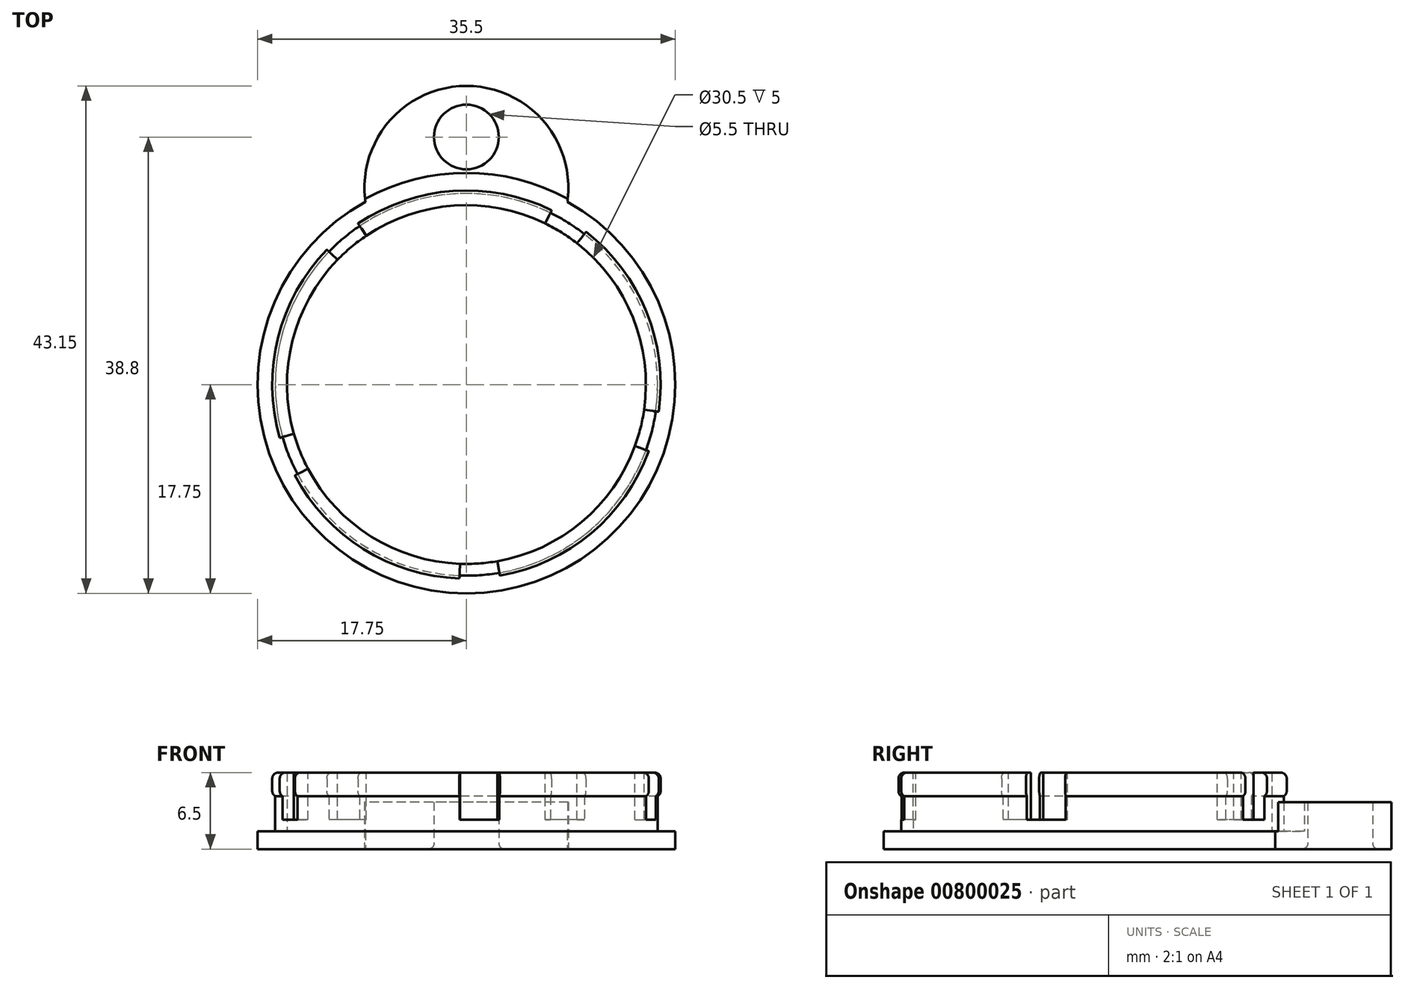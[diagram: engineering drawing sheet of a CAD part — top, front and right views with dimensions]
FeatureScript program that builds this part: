
annotation { "Feature Type Name" : "Feature", "Feature Type Description" : "" }
export const myFeature = defineFeature(function(context is Context, id is Id, definition is map)
    precondition{}
    {
        {
            var Q0;
            Q0=qCreatedBy(makeId("Top.planeOp"),FACE);
            var sketch = newSketch(context, id + "F0", { "sketchPlane" : qUnion([Q0])});
            skCircle(sketch, "E0", {"center": v(0, 0) * mm, "radius": 17.75 * mm});
            skLineSegment(sketch, "E1", {"start": v(-30.05, 0) * mm, "end": v(29.32, 0) * mm, "construction": true});
            skLineSegment(sketch, "E2", {"start": v(0, 26.58) * mm, "end": v(0, -26.58) * mm, "construction": true});
            skArc(sketch, "E3", {"start": v(0, 25.4) * mm, "mid": v(-6.53, 22.42) * mm, "end": v(-8.58, 15.54) * mm});
            skArc(sketch, "E4.MirrorCS", {"start": v(0, 25.4) * mm, "mid": v(6.53, 22.42) * mm, "end": v(8.58, 15.54) * mm});
            skCircle(sketch, "E5", {"center": v(0, 21.05) * mm, "radius": 2.75 * mm});
            skSolve(sketch);
        }
        {
            var Q0;
            {var subQ0=sQuery(id+"F0.wireOp",EDGE,"E0");var subQ1=makeQuery(id+"F0.imprint","INTERSECT",VERTEX,{"derivedFrom":[subQ0,sQuery(id+"F0.wireOp",EDGE,"E3")]});Q0=makeQuery(id+"F0.imprint","IMPRINT",FACE,{"disambiguationData":[TD([[makeQuery(id+"F0.imprint","IMPRINT",EDGE,{"disambiguationData":[TD([[subQ1,1.0]])],"derivedFrom":subQ0}),1.0]])]});}
            var Q1;
            {var subQ0=sQuery(id+"F0.wireOp",EDGE,"E3");Q1=makeQuery(id+"F0.imprint","IMPRINT",FACE,{"disambiguationData":[TD([[makeQuery(id+"F0.imprint","IMPRINT",EDGE,{"derivedFrom":subQ0}),1.0]])]});}
            extrude(context, id + "F1", {"entities" : qUnion([Q0, Q1]), "depth" : 1.5 * mm, "offsetDistance" : 25 * mm});
        }
        {
            var Q0;
            Q0=makeQuery(id+"F1.opExtrude","CAP_FACE",FACE,{"disambiguationData":[OSD([sQuery(id+"F0.wireOp",EDGE,"E0"),sQuery(id+"F0.wireOp",EDGE,"E3"),sQuery(id+"F0.wireOp",EDGE,"E4.MirrorCS"),sQuery(id+"F0.wireOp",EDGE,"E5")])],"isStart":false});
            var sketch = newSketch(context, id + "F2", { "sketchPlane" : qUnion([Q0])});
            skCircle(sketch, "E6", {"center": v(0, 0) * mm, "radius": 15.25 * mm});
            skCircle(sketch, "E7", {"center": v(0, 0) * mm, "radius": 16.25 * mm});
            skSolve(sketch);
        }
        {
            var Q0;
            Q0=makeQuery(id+"F2.imprint","IMPRINT",FACE,{"disambiguationData":[TD([[makeQuery(id+"F2.imprint","IMPRINT",EDGE,{"derivedFrom":sQuery(id+"F2.wireOp",EDGE,"E6")}),-1.0]])]});
            extrude(context, id + "F3", {"entities" : qUnion([Q0]), "operationType" : NewBodyOperationType.ADD, "depth" : 3 * mm, "offsetDistance" : 25 * mm});
        }
        {
            var Q0;
            {var subQ0=sQuery(id+"F0.wireOp",EDGE,"E0");var subQ1=sQuery(id+"F0.wireOp",EDGE,"E4.MirrorCS");var subQ2=sQuery(id+"F0.wireOp",EDGE,"E3");var subQ3=sQuery(id+"F0.wireOp",EDGE,"E5");Q0=makeQuery(id+"F3.boolean.opBoolean","SPLIT",FACE,{"disambiguationData":[TD([makeQuery(id+"F1.opExtrude","SWEPT_FACE",FACE,{"disambiguationData":[OSD([subQ0])]})])],"derivedFrom":makeQuery(id+"F1.opExtrude","CAP_FACE",FACE,{"disambiguationData":[OSD([subQ0,subQ2,subQ1,subQ3])],"isStart":false})});}
            var sketch = newSketch(context, id + "F4", { "sketchPlane" : qUnion([Q0])});
            skArc(sketch, "E8", {"start": v(8.58, 15.54) * mm, "mid": v(0, 25.4) * mm, "end": v(-8.58, 15.54) * mm});
            skArc(sketch, "E9", {"start": v(8.61, 15.8) * mm, "mid": v(0, 18) * mm, "end": v(-8.61, 15.8) * mm});
            skSolve(sketch);
        }
        {
            var Q0;
            {var subQ0=sQuery(id+"F4.wireOp",EDGE,"E9");Q0=makeQuery(id+"F4.imprint","IMPRINT",FACE,{"disambiguationData":[TD([[makeQuery(id+"F4.imprint","IMPRINT",EDGE,{"derivedFrom":subQ0}),-1.0]])]});}
            extrude(context, id + "F5", {"entities" : qUnion([Q0]), "operationType" : NewBodyOperationType.ADD, "depth" : 2.5 * mm, "offsetDistance" : 25 * mm});
        }
        {
            var Q0;
            Q0=makeQuery(id+"F3.opExtrude","CAP_FACE",FACE,{"disambiguationData":[OSD([sQuery(id+"F2.wireOp",EDGE,"E6"),sQuery(id+"F2.wireOp",EDGE,"E7")])],"isStart":false});
            var sketch = newSketch(context, id + "F6", { "sketchPlane" : qUnion([Q0])});
            skCircle(sketch, "E10", {"center": v(0, 0) * mm, "radius": 15.25 * mm});
            skCircle(sketch, "E11", {"center": v(0, 0) * mm, "radius": 16.5 * mm});
            skSolve(sketch);
        }
        {
            var Q0;
            Q0=makeQuery(id+"F6.imprint","IMPRINT",FACE,{"disambiguationData":[TD([[makeQuery(id+"F6.imprint","IMPRINT",EDGE,{"derivedFrom":sQuery(id+"F6.wireOp",EDGE,"E10")}),-1.0]])]});
            var Q1;
            Q1=makeQuery(id+"F6.imprint","IMPRINT",FACE,{"disambiguationData":[TD([[makeQuery(id+"F6.imprint","IMPRINT",EDGE,{"derivedFrom":sQuery(id+"F6.wireOp",EDGE,"E11")}),1.0]])]});
            extrude(context, id + "F7", {"entities" : qUnion([Q0, Q1]), "operationType" : NewBodyOperationType.ADD, "depth" : 2 * mm, "offsetDistance" : 25 * mm});
        }
        {
            var Q0;
            Q0=makeQuery(id+"F7.opExtrude","CAP_EDGE",EDGE,{"disambiguationData":[OSD([sQuery(id+"F6.wireOp",EDGE,"E11")])],"isStart":false});
            var Q1;
            Q1=makeQuery(id+"F7.opExtrude","CAP_EDGE",EDGE,{"disambiguationData":[OSD([sQuery(id+"F6.wireOp",EDGE,"E11")])],"isStart":true});
            fillet(context, id + "F8", {"entities" : qUnion([Q0, Q1]), "radius" : 0.5 * mm, "tangentPropagation" : true, "allowEdgeOverflow" : false});
        }
        {
            var Q0;
            Q0=makeQuery(id+"F7.opExtrude","CAP_FACE",FACE,{"disambiguationData":[OSD([sQuery(id+"F6.wireOp",EDGE,"E10"),sQuery(id+"F6.wireOp",EDGE,"E11")])],"isStart":false});
            var sketch = newSketch(context, id + "F9", { "sketchPlane" : qUnion([Q0])});
            skCircle(sketch, "E12.cCircle", {"center": v(0, 0) * mm, "radius": 17.3 * mm, "construction": true});
            skLineSegment(sketch, "E12.0", {"start": v(-14.74, 9.23) * mm, "end": v(-12.5, 12.1) * mm});
            skLineSegment(sketch, "E12.1", {"start": v(-12.5, 12.1) * mm, "end": v(-9.71, 14.43) * mm});
            skLineSegment(sketch, "E12.2", {"start": v(-9.71, 14.43) * mm, "end": v(-6.5, 16.13) * mm});
            skLineSegment(sketch, "E12.3", {"start": v(-6.5, 16.13) * mm, "end": v(-3, 17.13) * mm});
            skLineSegment(sketch, "E12.4", {"start": v(-3, 17.13) * mm, "end": v(0.63, 17.38) * mm});
            skLineSegment(sketch, "E12.5", {"start": v(0.63, 17.38) * mm, "end": v(4.23, 16.87) * mm});
            skLineSegment(sketch, "E12.6", {"start": v(4.23, 16.87) * mm, "end": v(7.64, 15.62) * mm});
            skLineSegment(sketch, "E12.7", {"start": v(7.64, 15.62) * mm, "end": v(10.72, 13.7) * mm});
            skLineSegment(sketch, "E12.8", {"start": v(10.72, 13.7) * mm, "end": v(13.34, 11.17) * mm});
            skLineSegment(sketch, "E12.9", {"start": v(13.34, 11.17) * mm, "end": v(15.37, 8.15) * mm});
            skLineSegment(sketch, "E12.10", {"start": v(15.37, 8.15) * mm, "end": v(16.73, 4.78) * mm});
            skLineSegment(sketch, "E12.11", {"start": v(16.73, 4.78) * mm, "end": v(17.35, 1.2) * mm});
            skLineSegment(sketch, "E12.12", {"start": v(17.35, 1.2) * mm, "end": v(17.22, -2.44) * mm});
            skLineSegment(sketch, "E12.13", {"start": v(17.22, -2.44) * mm, "end": v(16.34, -5.97) * mm});
            skLineSegment(sketch, "E12.14", {"start": v(16.34, -5.97) * mm, "end": v(14.74, -9.23) * mm});
            skLineSegment(sketch, "E12.15", {"start": v(14.74, -9.23) * mm, "end": v(12.5, -12.1) * mm});
            skLineSegment(sketch, "E12.16", {"start": v(12.5, -12.1) * mm, "end": v(9.71, -14.43) * mm});
            skLineSegment(sketch, "E12.17", {"start": v(9.71, -14.43) * mm, "end": v(6.5, -16.13) * mm});
            skLineSegment(sketch, "E12.18", {"start": v(6.5, -16.13) * mm, "end": v(3, -17.13) * mm});
            skLineSegment(sketch, "E12.19", {"start": v(3, -17.13) * mm, "end": v(-0.63, -17.38) * mm});
            skLineSegment(sketch, "E12.20", {"start": v(-0.63, -17.38) * mm, "end": v(-4.23, -16.87) * mm});
            skLineSegment(sketch, "E12.21", {"start": v(-4.23, -16.87) * mm, "end": v(-7.64, -15.62) * mm});
            skLineSegment(sketch, "E12.22", {"start": v(-7.64, -15.62) * mm, "end": v(-10.72, -13.7) * mm});
            skLineSegment(sketch, "E12.23", {"start": v(-10.72, -13.7) * mm, "end": v(-13.34, -11.17) * mm});
            skLineSegment(sketch, "E12.24", {"start": v(-13.34, -11.17) * mm, "end": v(-15.37, -8.15) * mm});
            skLineSegment(sketch, "E12.25", {"start": v(-15.37, -8.15) * mm, "end": v(-16.73, -4.78) * mm});
            skLineSegment(sketch, "E12.26", {"start": v(-16.73, -4.78) * mm, "end": v(-17.35, -1.2) * mm});
            skLineSegment(sketch, "E12.27", {"start": v(-17.35, -1.2) * mm, "end": v(-17.22, 2.44) * mm});
            skLineSegment(sketch, "E12.28", {"start": v(-17.22, 2.44) * mm, "end": v(-16.34, 5.97) * mm});
            skLineSegment(sketch, "E12.29", {"start": v(-16.34, 5.97) * mm, "end": v(-14.74, 9.23) * mm});
            skPoint(sketch, "E12.0.midPoint", {"position": v(-13.62, 10.67) * mm});
            skLineSegment(sketch, "E13", {"start": v(0, 0) * mm, "end": v(0.63, 21) * mm});
            skLineSegment(sketch, "E14", {"start": v(0, 0) * mm, "end": v(4.23, 16.87) * mm});
            skLineSegment(sketch, "E15", {"start": v(0, 0) * mm, "end": v(7.64, 15.62) * mm});
            skLineSegment(sketch, "E16", {"start": v(0, 0) * mm, "end": v(10.72, 13.7) * mm});
            skLineSegment(sketch, "E17", {"start": v(0, 0) * mm, "end": v(13.34, 11.17) * mm});
            skLineSegment(sketch, "E18", {"start": v(0, 0) * mm, "end": v(15.37, 8.15) * mm});
            skLineSegment(sketch, "E19", {"start": v(0, 0) * mm, "end": v(16.73, 4.78) * mm});
            skLineSegment(sketch, "E20", {"start": v(0, 0) * mm, "end": v(17.35, 1.2) * mm});
            skLineSegment(sketch, "E21", {"start": v(0, 0) * mm, "end": v(17.22, -2.44) * mm});
            skLineSegment(sketch, "E22", {"start": v(0, 0) * mm, "end": v(16.34, -5.97) * mm});
            skLineSegment(sketch, "E23", {"start": v(0, 0) * mm, "end": v(14.74, -9.23) * mm});
            skLineSegment(sketch, "E24", {"start": v(0, 0) * mm, "end": v(12.5, -12.1) * mm});
            skLineSegment(sketch, "E25", {"start": v(0, 0) * mm, "end": v(9.71, -14.43) * mm});
            skLineSegment(sketch, "E26", {"start": v(0, 0) * mm, "end": v(6.5, -16.13) * mm});
            skLineSegment(sketch, "E27", {"start": v(0, 0) * mm, "end": v(3, -17.13) * mm});
            skLineSegment(sketch, "E28", {"start": v(0, 0) * mm, "end": v(-0.63, -17.38) * mm});
            skLineSegment(sketch, "E29", {"start": v(0, 0) * mm, "end": v(-4.23, -16.87) * mm});
            skLineSegment(sketch, "E30", {"start": v(0, 0) * mm, "end": v(-7.64, -15.62) * mm});
            skLineSegment(sketch, "E31", {"start": v(0, 0) * mm, "end": v(-10.72, -13.7) * mm});
            skLineSegment(sketch, "E32", {"start": v(0, 0) * mm, "end": v(-13.34, -11.17) * mm});
            skLineSegment(sketch, "E33", {"start": v(0, 0) * mm, "end": v(-15.37, -8.15) * mm});
            skLineSegment(sketch, "E34", {"start": v(0, 0) * mm, "end": v(-16.73, -4.78) * mm});
            skLineSegment(sketch, "E35", {"start": v(0, 0) * mm, "end": v(-17.35, -1.2) * mm});
            skLineSegment(sketch, "E36", {"start": v(0, 0) * mm, "end": v(-3.36, -0.23) * mm});
            skLineSegment(sketch, "E37", {"start": v(0, 0) * mm, "end": v(-17.22, 2.44) * mm});
            skLineSegment(sketch, "E38", {"start": v(0, 0) * mm, "end": v(-16.34, 5.97) * mm});
            skLineSegment(sketch, "E39", {"start": v(0, 0) * mm, "end": v(-14.74, 9.23) * mm});
            skLineSegment(sketch, "E40", {"start": v(0, 0) * mm, "end": v(-12.5, 12.1) * mm});
            skLineSegment(sketch, "E41", {"start": v(0, 0) * mm, "end": v(-9.71, 14.43) * mm});
            skLineSegment(sketch, "E42", {"start": v(0, 0) * mm, "end": v(-6.5, 16.13) * mm});
            skLineSegment(sketch, "E43", {"start": v(0, 0) * mm, "end": v(-3, 17.13) * mm});
            skSolve(sketch);
        }
        {
            var Q0;
            {var subQ0=sQuery(id+"F9.wireOp",EDGE,"E15");var subQ1=sQuery(id+"F6.wireOp",EDGE,"E10");var subQ2=makeQuery(id+"F7.opExtrude","CAP_EDGE",EDGE,{"disambiguationData":[OSD([subQ1])],"isStart":false});var subQ3=makeQuery(id+"F9.imprint","INTERSECT",VERTEX,{"derivedFrom":[subQ2,subQ0]});Q0=makeQuery(id+"F9.imprint","IMPRINT",FACE,{"disambiguationData":[TD([[makeQuery(id+"F9.imprint","IMPRINT",EDGE,{"disambiguationData":[TD([[subQ3,1.0]])],"derivedFrom":subQ2}),-1.0]])]});}
            var Q1;
            {var subQ0=sQuery(id+"F9.wireOp",EDGE,"E12.7");Q1=makeQuery(id+"F9.imprint","IMPRINT",FACE,{"disambiguationData":[TD([[makeQuery(id+"F9.imprint","IMPRINT",EDGE,{"derivedFrom":subQ0}),-1.0]])]});}
            var Q2;
            {var subQ0=sQuery(id+"F9.wireOp",EDGE,"E21");var subQ1=sQuery(id+"F6.wireOp",EDGE,"E10");var subQ2=makeQuery(id+"F7.opExtrude","CAP_EDGE",EDGE,{"disambiguationData":[OSD([subQ1])],"isStart":false});var subQ3=makeQuery(id+"F9.imprint","INTERSECT",VERTEX,{"derivedFrom":[subQ2,subQ0]});Q2=makeQuery(id+"F9.imprint","IMPRINT",FACE,{"disambiguationData":[TD([[makeQuery(id+"F9.imprint","IMPRINT",EDGE,{"disambiguationData":[TD([[subQ3,1.0]])],"derivedFrom":subQ2}),-1.0]])]});}
            var Q3;
            {var subQ0=sQuery(id+"F9.wireOp",EDGE,"E12.13");Q3=makeQuery(id+"F9.imprint","IMPRINT",FACE,{"disambiguationData":[TD([[makeQuery(id+"F9.imprint","IMPRINT",EDGE,{"derivedFrom":subQ0}),-1.0]])]});}
            var Q4;
            {var subQ0=sQuery(id+"F9.wireOp",EDGE,"E27");var subQ1=sQuery(id+"F6.wireOp",EDGE,"E10");var subQ2=makeQuery(id+"F7.opExtrude","CAP_EDGE",EDGE,{"disambiguationData":[OSD([subQ1])],"isStart":false});var subQ3=makeQuery(id+"F9.imprint","INTERSECT",VERTEX,{"derivedFrom":[subQ2,subQ0]});Q4=makeQuery(id+"F9.imprint","IMPRINT",FACE,{"disambiguationData":[TD([[makeQuery(id+"F9.imprint","IMPRINT",EDGE,{"disambiguationData":[TD([[subQ3,1.0]])],"derivedFrom":subQ2}),-1.0]])]});}
            var Q5;
            {var subQ0=sQuery(id+"F9.wireOp",EDGE,"E12.19");Q5=makeQuery(id+"F9.imprint","IMPRINT",FACE,{"disambiguationData":[TD([[makeQuery(id+"F9.imprint","IMPRINT",EDGE,{"derivedFrom":subQ0}),-1.0]])]});}
            var Q6;
            {var subQ0=sQuery(id+"F9.wireOp",EDGE,"E33");var subQ1=sQuery(id+"F6.wireOp",EDGE,"E10");var subQ2=makeQuery(id+"F7.opExtrude","CAP_EDGE",EDGE,{"disambiguationData":[OSD([subQ1])],"isStart":false});var subQ3=makeQuery(id+"F9.imprint","INTERSECT",VERTEX,{"derivedFrom":[subQ2,subQ0]});Q6=makeQuery(id+"F9.imprint","IMPRINT",FACE,{"disambiguationData":[TD([[makeQuery(id+"F9.imprint","IMPRINT",EDGE,{"disambiguationData":[TD([[subQ3,1.0]])],"derivedFrom":subQ2}),-1.0]])]});}
            var Q7;
            {var subQ0=sQuery(id+"F9.wireOp",EDGE,"E12.25");Q7=makeQuery(id+"F9.imprint","IMPRINT",FACE,{"disambiguationData":[TD([[makeQuery(id+"F9.imprint","IMPRINT",EDGE,{"derivedFrom":subQ0}),-1.0]])]});}
            var Q8;
            {var subQ0=sQuery(id+"F9.wireOp",EDGE,"E40");var subQ1=sQuery(id+"F6.wireOp",EDGE,"E10");var subQ2=makeQuery(id+"F7.opExtrude","CAP_EDGE",EDGE,{"disambiguationData":[OSD([subQ1])],"isStart":false});var subQ3=makeQuery(id+"F9.imprint","INTERSECT",VERTEX,{"derivedFrom":[subQ2,subQ0]});Q8=makeQuery(id+"F9.imprint","IMPRINT",FACE,{"disambiguationData":[TD([[makeQuery(id+"F9.imprint","IMPRINT",EDGE,{"disambiguationData":[TD([[subQ3,1.0]])],"derivedFrom":subQ2}),-1.0]])]});}
            var Q9;
            {var subQ0=sQuery(id+"F9.wireOp",EDGE,"E12.1");Q9=makeQuery(id+"F9.imprint","IMPRINT",FACE,{"disambiguationData":[TD([[makeQuery(id+"F9.imprint","IMPRINT",EDGE,{"derivedFrom":subQ0}),-1.0]])]});}
            extrude(context, id + "F10", {"entities" : qUnion([Q0, Q1, Q2, Q3, Q4, Q5, Q6, Q7, Q8, Q9]), "operationType" : NewBodyOperationType.REMOVE, "oppositeDirection" : true, "depth" : 4 * mm, "offsetDistance" : 25 * mm});
        }
        {
            var Q0;
            Q0=makeQuery(id+"F1.opExtrude","CAP_EDGE",EDGE,{"disambiguationData":[OSD([sQuery(id+"F0.wireOp",EDGE,"E5")])],"isStart":true});
            fillet(context, id + "F11", {"entities" : qUnion([Q0]), "radius" : 0.5 * mm, "tangentPropagation" : true, "allowEdgeOverflow" : false});
        }
    });
